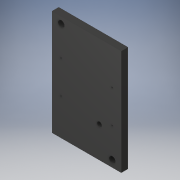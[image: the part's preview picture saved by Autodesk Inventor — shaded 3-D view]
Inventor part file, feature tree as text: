
AUTODESK INVENTOR PART (.ipt)
format: ipt  version: 2017 (Build 210142000, 142)  size: 184,832 bytes
history: native  units: in
note: dims shown in document units (in); Inventor stores cm internally (conversion verified against a paired STEP export)
features: sketch x4, extrude x4
ambient origin geometry x8: Origin, YZ Plane, XZ Plane, XY Plane, X Axis, Y Axis, Z Axis, Center Point
bodies: Body1 (feature_tree)
feature tree (8):
  sketch  "Sketch1"  dims[d0=1.9375in d1=1.25in]
  extrude  "Extrusion2"  Depth=1.25in
  extrude  "Extrusion3"  Depth=1.25in
  extrude  "Extrusion4"  Depth=0.25in
  extrude  "Extrusion5"  Depth=0.125in
  sketch  "Sketch7"  dims[d11=0.25in d12=0.25in]
  sketch  "Sketch8"  dims[d13=2.5in d14=2.125in d25=1.45in d26=1.45in d27=0.0625in d28=1.125in d29=1.125in d30=0.25in d31=0.25in d32=2.625in d33=4.0in d34=1.9375in d35=1.25in d36=0.0625in d37=1.9375in d38=1.25in d39=0.25in d40=0.25in d41=2.5in d42=2.125in d43=1.45in d44=1.45in d45=0.0625in d46=1.125in d47=1.125in d48=0.25in d49=0.25in d50=2.625in d51=4.0in d114=0.25in d115=0.0in d116=0.25in d117=0.0in d118=0.1875in d119=0.1875in d120=0.1875in d121=0.0625in d122=0.0in d123=0.1875in d124=0.125in d125=0.0in]
  sketch  "Sketch3"  dims[d2=0.0625in d3=0.7874in d5=1.9375in d6=0.7874in d8=1.25in]
